# Revit family: Electronics_Commercial-Loudspeakers_Biamp_Compact-Compression-Driver-Horn_MP26
name_source: partatom
category: Communication Devices
units: mm (PartAtom-declared; Revit-internal decimal feet)

## family parameters
Cut with Voids When Loaded = No
Host = Face
Maintain Annotation Orientation = No
OmniClass Number = 23.85.10.11.14.14.14
Part Type = Normal
Room Calculation Point = No
Round Connector Dimension = Use Diameter
Shared = No

## types (1)
- MP26-G
    100V transformer power taps in watts = 26 - 20 - 10
    Applicable in 100V = Yes
    Bracket Material = Biamp - Metal - Gray
    Closest RAL colour (subject to deviations) = RAL9006
    Colour = Grey
    Connector Description = Conductor; 26-20-10 W 100V
    Default Elevation = 4' - 0"
    Depth = 0' - 10 1/2"
    Description = MP26-G Powerful Sound Projector
    Frequency response in Hz = 90 - 19 k
    Grille main material = Aluminium
    Height = 0' - 6 1/2"
    Housing Material = Biamp - Plastic - Gray
    IP rating = 56
    Loudspeaker system = Dual cone
    Main construction material = ABS plastic
    Manufacturer = Biamp
    Max SPL 1m in dB = 107
    Model = MP26-G
    Mounting system = U-bracket
    Product Documentation Link = https://downloads.biamp.com
    Product Page URL = https://www.biamp.com
    Product data url = https://bimobject.com
    SPL 1W/1m in dB = 92
    URL = https://www.biamp.com
    Vertical dispersion angle 1000 Hz = 180°
    Weight = 4.19 lb
    Width = 0' - 7 1/2"
    Woofer cone material = Coated paper
    Woofer size in inch = 6.5

## geometry (parser evidence)
native form markers: Sweep x5
no freeform markers — native parametric forms only
